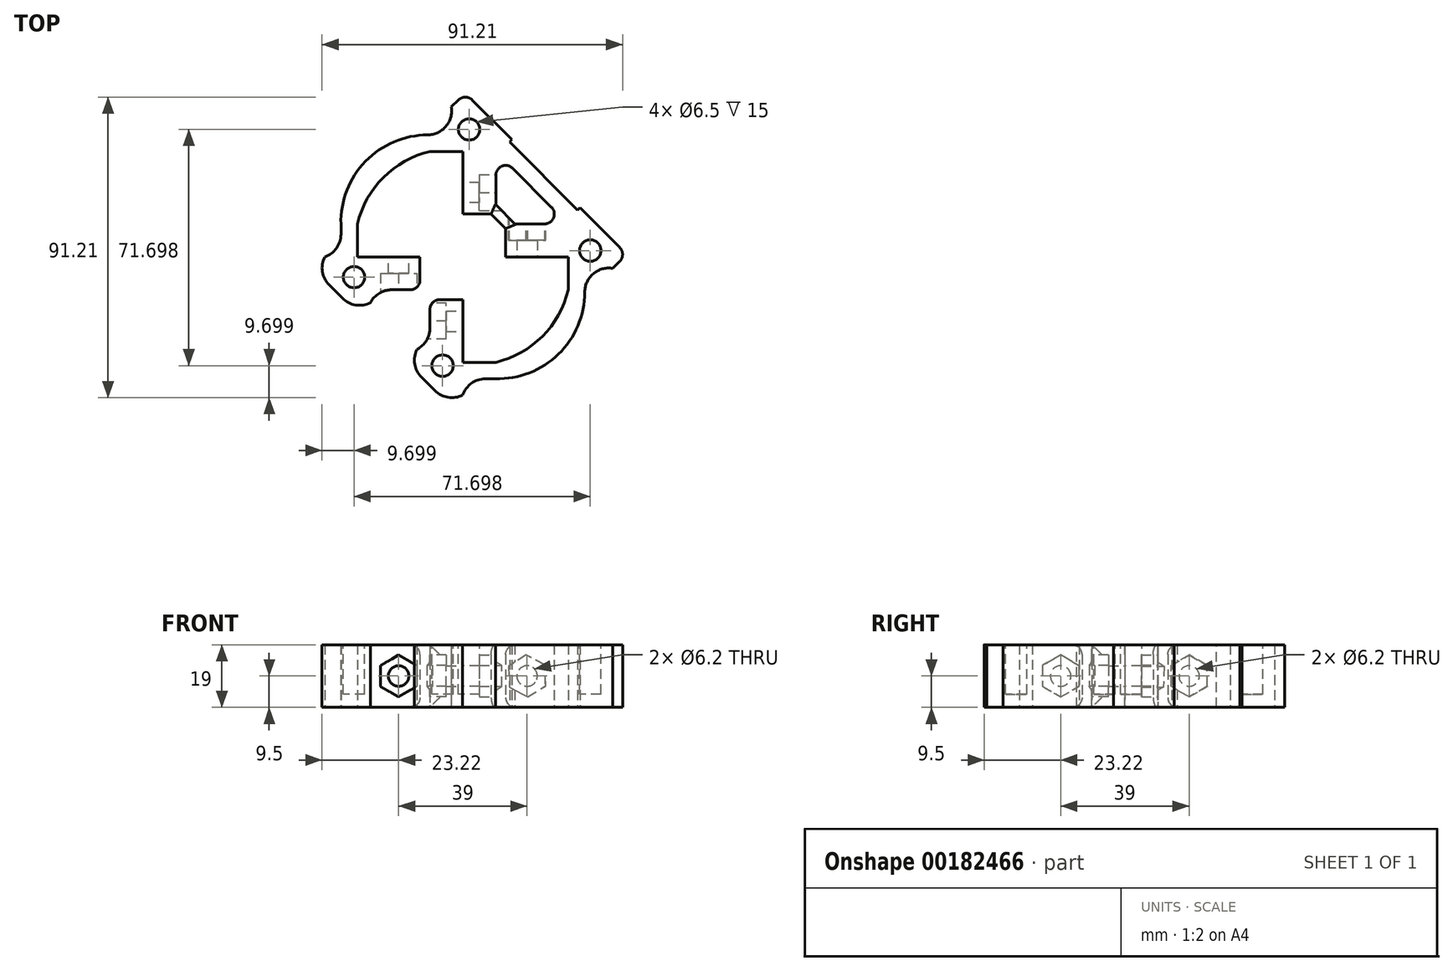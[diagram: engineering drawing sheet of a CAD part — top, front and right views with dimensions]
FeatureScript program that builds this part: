
annotation { "Feature Type Name" : "Feature", "Feature Type Description" : "" }
export const myFeature = defineFeature(function(context is Context, id is Id, definition is map)
    precondition{}
    {
        {
            var Q0;
            Q0=qCreatedBy(makeId("Top.planeOp"),FACE);
            var sketch = newSketch(context, id + "F0", { "sketchPlane" : qUnion([Q0])});
            skLineSegment(sketch, "E0.bottom", {"start": v(13, 13) * mm, "end": v(-13, 13) * mm, "construction": true});
            skLineSegment(sketch, "E0.top", {"start": v(13, -13) * mm, "end": v(-13, -13) * mm, "construction": true});
            skLineSegment(sketch, "E0.left", {"start": v(13, 13) * mm, "end": v(13, -13) * mm, "construction": true});
            skLineSegment(sketch, "E0.right", {"start": v(-13, 13) * mm, "end": v(-13, -13) * mm, "construction": true});
            skPoint(sketch, "E0.middle", {"position": v(0, 0) * mm});
            skLineSegment(sketch, "E1.bottom", {"start": v(13, 0) * mm, "end": v(32, 0) * mm});
            skLineSegment(sketch, "E1.top", {"start": v(13, 10) * mm, "end": v(32, 10) * mm});
            skLineSegment(sketch, "E1.left", {"start": v(13, 0) * mm, "end": v(13, 10) * mm});
            skLineSegment(sketch, "E1.right", {"start": v(32, 0) * mm, "end": v(32, 10) * mm});
            skLineSegment(sketch, "E2.bottom", {"start": v(0, 13) * mm, "end": v(10, 13) * mm});
            skLineSegment(sketch, "E2.top", {"start": v(0, 32) * mm, "end": v(10, 32) * mm});
            skLineSegment(sketch, "E2.left", {"start": v(0, 13) * mm, "end": v(0, 32) * mm});
            skLineSegment(sketch, "E2.right", {"start": v(10, 13) * mm, "end": v(10, 32) * mm});
            skLineSegment(sketch, "E3.bottom", {"start": v(0, -13) * mm, "end": v(-10, -13) * mm});
            skLineSegment(sketch, "E3.top", {"start": v(0, -32) * mm, "end": v(-10, -32) * mm});
            skLineSegment(sketch, "E3.left", {"start": v(0, -13) * mm, "end": v(0, -32) * mm});
            skLineSegment(sketch, "E3.right", {"start": v(-10, -13) * mm, "end": v(-10, -32) * mm});
            skLineSegment(sketch, "E4.bottom", {"start": v(-13, 0) * mm, "end": v(-32, 0) * mm});
            skLineSegment(sketch, "E4.top", {"start": v(-13, -10) * mm, "end": v(-32, -10) * mm});
            skLineSegment(sketch, "E4.left", {"start": v(-13, 0) * mm, "end": v(-13, -10) * mm});
            skLineSegment(sketch, "E4.right", {"start": v(-32, 0) * mm, "end": v(-32, -10) * mm});
            skLineSegment(sketch, "E5", {"start": v(32, 0) * mm, "end": v(32, -10) * mm});
            skLineSegment(sketch, "E6", {"start": v(0, -32) * mm, "end": v(10, -32) * mm});
            skLineSegment(sketch, "E7", {"start": v(-32, 0) * mm, "end": v(-32, 10) * mm});
            skLineSegment(sketch, "E8", {"start": v(0, 32) * mm, "end": v(-10, 32) * mm});
            skArc(sketch, "E9", {"start": v(10, -32) * mm, "mid": v(25.74, -25.74) * mm, "end": v(32, -10) * mm, "construction": true});
            skArc(sketch, "E10", {"start": v(-10, 32) * mm, "mid": v(-25.74, 25.74) * mm, "end": v(-32, 10) * mm, "construction": true});
            skCircle(sketch, "E11", {"center": v(0, 0) * mm, "radius": 15 * mm, "construction": true});
            skLineSegment(sketch, "E12", {"start": v(10, 32) * mm, "end": v(32, 10) * mm});
            skLineSegment(sketch, "E13", {"start": v(-32, -10) * mm, "end": v(-10, -32) * mm});
            skLineSegment(sketch, "E14.0", {"start": v(-37, 0) * mm, "end": v(-37, -12.07) * mm});
            skLineSegment(sketch, "E14.1", {"start": v(37, 0) * mm, "end": v(37, -9.93) * mm});
            skArc(sketch, "E14.2", {"start": v(9.93, -37) * mm, "mid": v(29.28, -29.28) * mm, "end": v(37, -9.93) * mm});
            skLineSegment(sketch, "E14.3", {"start": v(0, -37) * mm, "end": v(9.93, -37) * mm});
            skLineSegment(sketch, "E14.4", {"start": v(0, -37) * mm, "end": v(-12.07, -37) * mm});
            skLineSegment(sketch, "E14.5", {"start": v(37, 0) * mm, "end": v(37, 12.07) * mm});
            skLineSegment(sketch, "E14.6", {"start": v(-37, -12.07) * mm, "end": v(-12.07, -37) * mm});
            skLineSegment(sketch, "E14.7", {"start": v(12.07, 37) * mm, "end": v(37, 12.07) * mm});
            skLineSegment(sketch, "E14.8", {"start": v(0, 37) * mm, "end": v(12.07, 37) * mm});
            skLineSegment(sketch, "E14.9", {"start": v(0, 37) * mm, "end": v(-9.93, 37) * mm});
            skArc(sketch, "E14.10", {"start": v(-9.93, 37) * mm, "mid": v(-29.28, 29.28) * mm, "end": v(-37, 9.93) * mm});
            skLineSegment(sketch, "E14.11", {"start": v(-37, 0) * mm, "end": v(-37, 9.93) * mm});
            skCircle(sketch, "E15", {"center": v(0, 0) * mm, "radius": 4.5 * mm, "construction": true});
            skArc(sketch, "E16", {"start": v(-10, 32) * mm, "mid": v(-24.12, 24.12) * mm, "end": v(-32, 10) * mm});
            skArc(sketch, "E17", {"start": v(10, -32) * mm, "mid": v(24.12, -24.12) * mm, "end": v(32, -10) * mm});
            skLineSegment(sketch, "E18", {"start": v(10, 13) * mm, "end": v(13, 10) * mm, "construction": true});
            skLineSegment(sketch, "E19", {"start": v(10, 15.83) * mm, "end": v(15.83, 10) * mm});
            skLineSegment(sketch, "E20", {"start": v(8.59, 13) * mm, "end": v(13, 8.59) * mm});
            skLineSegment(sketch, "E21", {"start": v(-21, -21) * mm, "end": v(-24.54, -24.54) * mm, "construction": true});
            skLineSegment(sketch, "E22.0", {"start": v(-28.07, -13.93) * mm, "end": v(-31.6, -17.46) * mm});
            skLineSegment(sketch, "E23.0", {"start": v(-13.93, -28.07) * mm, "end": v(-17.46, -31.6) * mm});
            skLineSegment(sketch, "E24", {"start": v(37, 12.07) * mm, "end": v(49.02, 0.05) * mm});
            skLineSegment(sketch, "E25", {"start": v(49.02, 0.05) * mm, "end": v(45.49, -3.49) * mm});
            skLineSegment(sketch, "E26", {"start": v(45.49, -3.49) * mm, "end": v(32, 10) * mm});
            skLineSegment(sketch, "E27", {"start": v(12.07, 37) * mm, "end": v(0.05, 49.02) * mm});
            skLineSegment(sketch, "E28", {"start": v(0.05, 49.02) * mm, "end": v(-3.49, 45.49) * mm});
            skLineSegment(sketch, "E29", {"start": v(-3.49, 45.49) * mm, "end": v(10, 32) * mm});
            skLineSegment(sketch, "E30", {"start": v(-12.07, -37) * mm, "end": v(-3.59, -45.49) * mm});
            skLineSegment(sketch, "E31", {"start": v(-3.59, -45.49) * mm, "end": v(-0.05, -41.95) * mm});
            skLineSegment(sketch, "E32", {"start": v(-0.05, -41.95) * mm, "end": v(-10, -32) * mm});
            skLineSegment(sketch, "E33", {"start": v(-37, -12.07) * mm, "end": v(-45.49, -3.59) * mm});
            skLineSegment(sketch, "E34", {"start": v(-45.49, -3.59) * mm, "end": v(-41.95, -0.05) * mm});
            skLineSegment(sketch, "E35", {"start": v(-41.95, -0.05) * mm, "end": v(-32, -10) * mm});
            skSolve(sketch);
        }
        {
            var Q0;
            Q0=makeQuery(id+"F0.imprint","IMPRINT",FACE,{"disambiguationData":[TD([[makeQuery(id+"F0.imprint","IMPRINT",EDGE,{"derivedFrom":sQuery(id+"F0.wireOp",EDGE,"E1.right")}),-1.0]])]});
            var Q1;
            Q1=makeQuery(id+"F0.imprint","IMPRINT",FACE,{"disambiguationData":[TD([[makeQuery(id+"F0.imprint","IMPRINT",EDGE,{"derivedFrom":sQuery(id+"F0.wireOp",EDGE,"E3.bottom")}),1.0]])]});
            var Q2;
            Q2=makeQuery(id+"F0.imprint","IMPRINT",FACE,{"disambiguationData":[TD([[makeQuery(id+"F0.imprint","IMPRINT",EDGE,{"derivedFrom":sQuery(id+"F0.wireOp",EDGE,"E1.bottom")}),1.0]])]});
            var Q3;
            Q3=makeQuery(id+"F0.imprint","IMPRINT",FACE,{"disambiguationData":[TD([[makeQuery(id+"F0.imprint","IMPRINT",EDGE,{"derivedFrom":sQuery(id+"F0.wireOp",EDGE,"E2.bottom")}),1.0]])]});
            var Q4;
            Q4=makeQuery(id+"F0.imprint","IMPRINT",FACE,{"disambiguationData":[TD([[makeQuery(id+"F0.imprint","IMPRINT",EDGE,{"derivedFrom":sQuery(id+"F0.wireOp",EDGE,"E4.bottom")}),1.0]])]});
            var Q5;
            {var subQ4=sQuery(id+"F0.wireOp",EDGE,"7QYkWqvo-aJCI-HwU7-Pkr0-dl33K8GSCUU7");Q5=makeQuery(id+"F0.imprint","IMPRINT",FACE,{"disambiguationData":[TD([[makeQuery(id+"F0.imprint","IMPRINT",EDGE,{"derivedFrom":subQ4}),-1.0]])]});}
            var Q6;
            {var subQ4=sQuery(id+"F0.wireOp",EDGE,"jUQw4thv-zTIx-3EJl-gbHM-SSJWuM9t6vhC");Q6=makeQuery(id+"F0.imprint","IMPRINT",FACE,{"disambiguationData":[TD([[makeQuery(id+"F0.imprint","IMPRINT",EDGE,{"derivedFrom":subQ4}),1.0]])]});}
            var Q7;
            {var subQ3=sQuery(id+"F0.wireOp",EDGE,"E19");Q7=makeQuery(id+"F0.imprint","IMPRINT",FACE,{"disambiguationData":[TD([[makeQuery(id+"F0.imprint","IMPRINT",EDGE,{"derivedFrom":subQ3}),-1.0]])]});}
            var Q8;
            {var subQ4=sQuery(id+"F0.wireOp",EDGE,"E12");Q8=makeQuery(id+"F0.imprint","IMPRINT",FACE,{"disambiguationData":[TD([[makeQuery(id+"F0.imprint","IMPRINT",EDGE,{"derivedFrom":subQ4}),1.0]])]});}
            var Q9;
            {var subQ0=sQuery(id+"F0.wireOp",EDGE,"E27");Q9=makeQuery(id+"F0.imprint","IMPRINT",FACE,{"disambiguationData":[TD([[makeQuery(id+"F0.imprint","IMPRINT",EDGE,{"derivedFrom":subQ0}),1.0]])]});}
            var Q10;
            {var subQ7=sQuery(id+"F0.wireOp",EDGE,"E2.top");Q10=makeQuery(id+"F0.imprint","IMPRINT",FACE,{"disambiguationData":[TD([[makeQuery(id+"F0.imprint","IMPRINT",EDGE,{"derivedFrom":subQ7}),1.0]])]});}
            var Q11;
            {var subQ0=sQuery(id+"F0.wireOp",EDGE,"E24");Q11=makeQuery(id+"F0.imprint","IMPRINT",FACE,{"disambiguationData":[TD([[makeQuery(id+"F0.imprint","IMPRINT",EDGE,{"derivedFrom":subQ0}),-1.0]])]});}
            var Q12;
            {var subQ0=sQuery(id+"F0.wireOp",EDGE,"E30");Q12=makeQuery(id+"F0.imprint","IMPRINT",FACE,{"disambiguationData":[TD([[makeQuery(id+"F0.imprint","IMPRINT",EDGE,{"derivedFrom":subQ0}),1.0]])]});}
            var Q13;
            {var subQ0=sQuery(id+"F0.wireOp",EDGE,"E33");Q13=makeQuery(id+"F0.imprint","IMPRINT",FACE,{"disambiguationData":[TD([[makeQuery(id+"F0.imprint","IMPRINT",EDGE,{"derivedFrom":subQ0}),-1.0]])]});}
            var Q14;
            {var subQ3=sQuery(id+"F0.wireOp",EDGE,"E23.0");Q14=makeQuery(id+"F0.imprint","IMPRINT",FACE,{"disambiguationData":[TD([[makeQuery(id+"F0.imprint","IMPRINT",EDGE,{"derivedFrom":subQ3}),1.0]])]});}
            var Q15;
            {var subQ0=sQuery(id+"F0.wireOp",EDGE,"E22.0");Q15=makeQuery(id+"F0.imprint","IMPRINT",FACE,{"disambiguationData":[TD([[makeQuery(id+"F0.imprint","IMPRINT",EDGE,{"derivedFrom":subQ0}),-1.0]])]});}
            extrude(context, id + "F1", {"entities" : qUnion([Q0, Q1, Q2, Q3, Q4, Q5, Q6, Q7, Q8, Q9, Q10, Q11, Q12, Q13, Q14, Q15]), "depth" : 19 * mm});
        }
        {
            var Q0;
            Q0=makeQuery(id+"F1.opExtrude","SWEPT_FACE",FACE,{"disambiguationData":[OSD([sQuery(id+"F0.wireOp",EDGE,"E3.right")])]});
            var sketch = newSketch(context, id + "F2", { "sketchPlane" : qUnion([Q0])});
            skLineSegment(sketch, "E36", {"start": v(19.5, 9.5) * mm, "end": v(32, 9.5) * mm, "construction": true});
            skCircle(sketch, "E37.cCircle", {"center": v(19.5, 9.5) * mm, "radius": 5.5 * mm, "construction": true});
            skLineSegment(sketch, "E37.0", {"start": v(14, 6.32) * mm, "end": v(14, 12.68) * mm});
            skLineSegment(sketch, "E37.1", {"start": v(14, 12.68) * mm, "end": v(19.5, 15.85) * mm});
            skLineSegment(sketch, "E37.2", {"start": v(19.5, 15.85) * mm, "end": v(25, 12.68) * mm});
            skLineSegment(sketch, "E37.3", {"start": v(25, 12.68) * mm, "end": v(25, 6.32) * mm});
            skLineSegment(sketch, "E37.4", {"start": v(25, 6.32) * mm, "end": v(19.5, 3.15) * mm});
            skLineSegment(sketch, "E37.5", {"start": v(19.5, 3.15) * mm, "end": v(14, 6.32) * mm});
            skPoint(sketch, "E37.0.midPoint", {"position": v(14, 9.5) * mm});
            skSolve(sketch);
        }
        {
            var Q0;
            Q0=makeQuery(id+"F2.imprint","IMPRINT",FACE,{"disambiguationData":[TD([[makeQuery(id+"F2.imprint","IMPRINT",EDGE,{"derivedFrom":sQuery(id+"F2.wireOp",EDGE,"E37.0")}),-1.0]])]});
            extrude(context, id + "F3", {"entities" : qUnion([Q0]), "operationType" : NewBodyOperationType.REMOVE, "oppositeDirection" : true, "depth" : 5 * mm});
        }
        {
            var Q0;
            Q0=makeQuery(id+"F1.opExtrude","SWEPT_FACE",FACE,{"disambiguationData":[OSD([sQuery(id+"F0.wireOp",EDGE,"E4.top")])]});
            var sketch = newSketch(context, id + "F4", { "sketchPlane" : qUnion([Q0])});
            skLineSegment(sketch, "E38", {"start": v(-32, 9.5) * mm, "end": v(-19.5, 9.5) * mm, "construction": true});
            skPoint(sketch, "E38.endSnap0", {"position": v(-32, 9.5) * mm});
            skCircle(sketch, "E39.cCircle", {"center": v(-19.5, 9.5) * mm, "radius": 5.5 * mm, "construction": true});
            skLineSegment(sketch, "E39.0", {"start": v(-14, 12.68) * mm, "end": v(-14, 6.32) * mm});
            skLineSegment(sketch, "E39.1", {"start": v(-14, 6.32) * mm, "end": v(-19.5, 3.15) * mm});
            skLineSegment(sketch, "E39.2", {"start": v(-19.5, 3.15) * mm, "end": v(-25, 6.32) * mm});
            skLineSegment(sketch, "E39.3", {"start": v(-25, 6.32) * mm, "end": v(-25, 12.68) * mm});
            skLineSegment(sketch, "E39.4", {"start": v(-25, 12.68) * mm, "end": v(-19.5, 15.85) * mm});
            skLineSegment(sketch, "E39.5", {"start": v(-19.5, 15.85) * mm, "end": v(-14, 12.68) * mm});
            skPoint(sketch, "E39.0.midPoint", {"position": v(-14, 9.5) * mm});
            skSolve(sketch);
        }
        {
            var Q0;
            Q0=makeQuery(id+"F4.imprint","IMPRINT",FACE,{"disambiguationData":[TD([[makeQuery(id+"F4.imprint","IMPRINT",EDGE,{"derivedFrom":sQuery(id+"F4.wireOp",EDGE,"E39.0")}),-1.0]])]});
            extrude(context, id + "F5", {"entities" : qUnion([Q0]), "operationType" : NewBodyOperationType.REMOVE, "oppositeDirection" : true, "depth" : 5 * mm});
        }
        {
            var Q0;
            Q0=makeQuery(id+"F1.opExtrude","SWEPT_FACE",FACE,{"disambiguationData":[OSD([sQuery(id+"F0.wireOp",EDGE,"E2.right")])]});
            var sketch = newSketch(context, id + "F6", { "sketchPlane" : qUnion([Q0])});
            skCircle(sketch, "E40.cCircle", {"center": v(19.5, 9.5) * mm, "radius": 5.5 * mm, "construction": true});
            skLineSegment(sketch, "E40.0", {"start": v(14, 6.32) * mm, "end": v(14, 12.68) * mm});
            skLineSegment(sketch, "E40.1", {"start": v(14, 12.68) * mm, "end": v(19.5, 15.85) * mm});
            skLineSegment(sketch, "E40.2", {"start": v(19.5, 15.85) * mm, "end": v(25, 12.68) * mm});
            skLineSegment(sketch, "E40.3", {"start": v(25, 12.68) * mm, "end": v(25, 6.32) * mm});
            skLineSegment(sketch, "E40.4", {"start": v(25, 6.32) * mm, "end": v(19.5, 3.15) * mm});
            skLineSegment(sketch, "E40.5", {"start": v(19.5, 3.15) * mm, "end": v(14, 6.32) * mm});
            skPoint(sketch, "E40.0.midPoint", {"position": v(14, 9.5) * mm});
            skSolve(sketch);
        }
        {
            var Q0;
            Q0=makeQuery(id+"F6.imprint","IMPRINT",FACE,{"disambiguationData":[TD([[makeQuery(id+"F6.imprint","IMPRINT",EDGE,{"derivedFrom":sQuery(id+"F6.wireOp",EDGE,"E40.0")}),-1.0]])]});
            var Q1;
            {var subQ1=sQuery(id+"F6.wireOp",EDGE,"E40.2");Q1=makeQuery(id+"F6.imprint","IMPRINT",FACE,{"disambiguationData":[TD([[makeQuery(id+"F6.imprint","IMPRINT",EDGE,{"derivedFrom":subQ1}),-1.0]])]});}
            extrude(context, id + "F7", {"entities" : qUnion([Q0, Q1]), "operationType" : NewBodyOperationType.REMOVE, "oppositeDirection" : true, "depth" : 10 * mm, "symmetric" : true});
        }
        {
            var Q0;
            Q0=makeQuery(id+"F1.opExtrude","SWEPT_FACE",FACE,{"disambiguationData":[OSD([sQuery(id+"F0.wireOp",EDGE,"E1.top")])]});
            var sketch = newSketch(context, id + "F8", { "sketchPlane" : qUnion([Q0])});
            skLineSegment(sketch, "E41", {"start": v(-32, 9.5) * mm, "end": v(-19.5, 9.5) * mm, "construction": true});
            skCircle(sketch, "E42.cCircle", {"center": v(-19.5, 9.5) * mm, "radius": 5.5 * mm, "construction": true});
            skLineSegment(sketch, "E42.0", {"start": v(-13.87, 12.45) * mm, "end": v(-14.13, 6.1) * mm});
            skLineSegment(sketch, "E42.1", {"start": v(-14.13, 6.1) * mm, "end": v(-19.76, 3.15) * mm});
            skLineSegment(sketch, "E42.2", {"start": v(-19.76, 3.15) * mm, "end": v(-25.13, 6.55) * mm});
            skLineSegment(sketch, "E42.3", {"start": v(-25.13, 6.55) * mm, "end": v(-24.87, 12.9) * mm});
            skLineSegment(sketch, "E42.4", {"start": v(-24.87, 12.9) * mm, "end": v(-19.24, 15.85) * mm});
            skLineSegment(sketch, "E42.5", {"start": v(-19.24, 15.85) * mm, "end": v(-13.87, 12.45) * mm});
            skPoint(sketch, "E42.0.midPoint", {"position": v(-14, 9.27) * mm});
            skSolve(sketch);
        }
        {
            var Q0;
            Q0=makeQuery(id+"F8.imprint","IMPRINT",FACE,{"disambiguationData":[TD([[makeQuery(id+"F8.imprint","IMPRINT",EDGE,{"derivedFrom":sQuery(id+"F8.wireOp",EDGE,"E42.0")}),-1.0]])]});
            var Q1;
            {var subQ6=sQuery(id+"F8.wireOp",EDGE,"E42.2");Q1=makeQuery(id+"F8.imprint","IMPRINT",FACE,{"disambiguationData":[TD([[makeQuery(id+"F8.imprint","IMPRINT",EDGE,{"derivedFrom":subQ6}),-1.0]])]});}
            extrude(context, id + "F9", {"entities" : qUnion([Q0, Q1]), "operationType" : NewBodyOperationType.REMOVE, "oppositeDirection" : true, "depth" : 10 * mm, "symmetric" : true});
        }
        {
            var Q0;
            Q0=sQuery(id+"F6.wireOp",VERTEX,"E40.cCircle.center");
            var Q1;
            Q1=sQuery(id+"F8.wireOp",VERTEX,"E41.end");
            var Q2;
            Q2=sQuery(id+"F2.wireOp",VERTEX,"E37.cCircle.center");
            var Q3;
            Q3=sQuery(id+"F4.wireOp",VERTEX,"E38.end");
            var Q4;
            Q4=makeQuery(id+"F1.opExtrude","SWEPT_BODY",BODY,{"disambiguationData":[OSD([sQuery(id+"F0.wireOp",EDGE,"E1.bottom"),sQuery(id+"F0.wireOp",EDGE,"E1.top"),sQuery(id+"F0.wireOp",EDGE,"E1.left"),sQuery(id+"F0.wireOp",EDGE,"E2.bottom"),sQuery(id+"F0.wireOp",EDGE,"E2.left"),sQuery(id+"F0.wireOp",EDGE,"E2.right"),sQuery(id+"F0.wireOp",EDGE,"E3.bottom"),sQuery(id+"F0.wireOp",EDGE,"E3.left"),sQuery(id+"F0.wireOp",EDGE,"E3.right"),sQuery(id+"F0.wireOp",EDGE,"E4.bottom"),sQuery(id+"F0.wireOp",EDGE,"E4.top"),sQuery(id+"F0.wireOp",EDGE,"E4.left"),sQuery(id+"F0.wireOp",EDGE,"E5"),sQuery(id+"F0.wireOp",EDGE,"E6"),sQuery(id+"F0.wireOp",EDGE,"E7"),sQuery(id+"F0.wireOp",EDGE,"E8"),sQuery(id+"F0.wireOp",EDGE,"E12"),sQuery(id+"F0.wireOp",EDGE,"E13"),sQuery(id+"F0.wireOp",EDGE,"E14.0"),sQuery(id+"F0.wireOp",EDGE,"E14.1"),sQuery(id+"F0.wireOp",EDGE,"E14.2"),sQuery(id+"F0.wireOp",EDGE,"E14.3"),sQuery(id+"F0.wireOp",EDGE,"E14.4"),sQuery(id+"F0.wireOp",EDGE,"E14.5"),sQuery(id+"F0.wireOp",EDGE,"E14.6"),sQuery(id+"F0.wireOp",EDGE,"E14.7"),sQuery(id+"F0.wireOp",EDGE,"E14.8"),sQuery(id+"F0.wireOp",EDGE,"E14.9"),sQuery(id+"F0.wireOp",EDGE,"E14.10"),sQuery(id+"F0.wireOp",EDGE,"E14.11"),sQuery(id+"F0.wireOp",EDGE,"E16"),sQuery(id+"F0.wireOp",EDGE,"E17"),sQuery(id+"F0.wireOp",EDGE,"E19"),sQuery(id+"F0.wireOp",EDGE,"E20"),sQuery(id+"F0.wireOp",EDGE,"E22.0"),sQuery(id+"F0.wireOp",EDGE,"E23.0"),sQuery(id+"F0.wireOp",EDGE,"7QYkWqvo-aJCI-HwU7-Pkr0-dl33K8GSCUU7"),sQuery(id+"F0.wireOp",EDGE,"UtTPwMuY-yqNM-BxKw-NphB-S71OTgtlkQoO"),sQuery(id+"F0.wireOp",EDGE,"jUQw4thv-zTIx-3EJl-gbHM-SSJWuM9t6vhC"),sQuery(id+"F0.wireOp",EDGE,"jgdTeO3I-7sCt-ISHI-VTCF-wijFFm9s4p1R"),sQuery(id+"F0.wireOp",EDGE,"E24"),sQuery(id+"F0.wireOp",EDGE,"E25"),sQuery(id+"F0.wireOp",EDGE,"E26"),sQuery(id+"F0.wireOp",EDGE,"E27"),sQuery(id+"F0.wireOp",EDGE,"E28"),sQuery(id+"F0.wireOp",EDGE,"E29")])]});
            hole(context, id + "F10", {"style" : HoleStyle.SIMPLE, "endStyle" : HoleEndStyle.BLIND, "holeDiameter" : 6.2 * mm, "holeDepth" : 10 * mm, "locations" : qUnion([Q0, Q1, Q2, Q3]), "scope" : qUnion([Q4])});
        }
        {
            var Q0;
            Q0=makeQuery(id+"F1.opExtrude","SWEPT_FACE",FACE,{"disambiguationData":[OSD([sQuery(id+"F0.wireOp",EDGE,"E14.7"),sQuery(id+"F0.wireOp",EDGE,"E24"),sQuery(id+"F0.wireOp",EDGE,"E27")])]});
            var sketch = newSketch(context, id + "F11", { "sketchPlane" : qUnion([Q0])});
            skLineSegment(sketch, "E43", {"start": v(-34.63, 19) * mm, "end": v(-34.63, 0) * mm});
            skLineSegment(sketch, "E44", {"start": v(34.63, 0) * mm, "end": v(34.63, 19) * mm});
            skLineSegment(sketch, "E45", {"start": v(-14.63, 19) * mm, "end": v(-14.63, 0) * mm});
            skLineSegment(sketch, "E46", {"start": v(14.63, 19) * mm, "end": v(14.63, 0) * mm});
            skSolve(sketch);
        }
        {
            var Q0;
            {var subQ0=sQuery(id+"F11.wireOp",EDGE,"E44");Q0=makeQuery(id+"F11.imprint","IMPRINT",FACE,{"disambiguationData":[TD([[makeQuery(id+"F11.imprint","IMPRINT",EDGE,{"derivedFrom":subQ0}),-1.0]])]});}
            var Q1;
            {var subQ0=sQuery(id+"F11.wireOp",EDGE,"E43");Q1=makeQuery(id+"F11.imprint","IMPRINT",FACE,{"disambiguationData":[TD([[makeQuery(id+"F11.imprint","IMPRINT",EDGE,{"derivedFrom":subQ0}),1.0]])]});}
            extrude(context, id + "F12", {"entities" : qUnion([Q0, Q1]), "operationType" : NewBodyOperationType.ADD, "depth" : 1 * mm});
        }
        {
            var Q0;
            Q0=makeQuery(id+"F1.opExtrude","SWEPT_EDGE",EDGE,{"disambiguationData":[OSD([sQuery(id+"F0.wireOp",EDGE,"E14.8"),sQuery(id+"F0.wireOp",EDGE,"E29")])]});
            var Q1;
            Q1=makeQuery(id+"F1.opExtrude","SWEPT_EDGE",EDGE,{"disambiguationData":[OSD([sQuery(id+"F0.wireOp",EDGE,"E14.5"),sQuery(id+"F0.wireOp",EDGE,"E26")])]});
            var Q2;
            Q2=makeQuery(id+"F12.opExtrude","CAP_EDGE",EDGE,{"disambiguationData":[OSD([sQuery(id+"F11.wireOp",EDGE,"E46")])],"isStart":true});
            var Q3;
            Q3=makeQuery(id+"F12.opExtrude","CAP_EDGE",EDGE,{"disambiguationData":[OSD([sQuery(id+"F11.wireOp",EDGE,"E45")])],"isStart":true});
            var Q4;
            Q4=makeQuery(id+"F1.opExtrude","SWEPT_EDGE",EDGE,{"disambiguationData":[OSD([sQuery(id+"F0.wireOp",EDGE,"E14.4"),sQuery(id+"F0.wireOp",EDGE,"E32")])]});
            var Q5;
            Q5=makeQuery(id+"F1.opExtrude","SWEPT_EDGE",EDGE,{"disambiguationData":[OSD([sQuery(id+"F0.wireOp",EDGE,"E14.0"),sQuery(id+"F0.wireOp",EDGE,"E35")])]});
            var Q6;
            Q6=makeQuery(id+"F1.opExtrude","SWEPT_EDGE",EDGE,{"disambiguationData":[OSD([sQuery(id+"F0.wireOp",EDGE,"E33"),sQuery(id+"F0.wireOp",EDGE,"E34")])]});
            var Q7;
            Q7=makeQuery(id+"F1.opExtrude","SWEPT_EDGE",EDGE,{"disambiguationData":[OSD([sQuery(id+"F0.wireOp",EDGE,"E14.6"),sQuery(id+"F0.wireOp",EDGE,"E22.0")])]});
            var Q8;
            Q8=makeQuery(id+"F1.opExtrude","SWEPT_EDGE",EDGE,{"disambiguationData":[OSD([sQuery(id+"F0.wireOp",EDGE,"E4.top"),sQuery(id+"F0.wireOp",EDGE,"E4.right"),sQuery(id+"F0.wireOp",EDGE,"E13"),sQuery(id+"F0.wireOp",EDGE,"E35")])]});
            var Q9;
            Q9=makeQuery(id+"F1.opExtrude","SWEPT_EDGE",EDGE,{"disambiguationData":[OSD([sQuery(id+"F0.wireOp",EDGE,"E3.top"),sQuery(id+"F0.wireOp",EDGE,"E3.right"),sQuery(id+"F0.wireOp",EDGE,"E13"),sQuery(id+"F0.wireOp",EDGE,"E32")])]});
            var Q10;
            Q10=makeQuery(id+"F1.opExtrude","SWEPT_EDGE",EDGE,{"disambiguationData":[OSD([sQuery(id+"F0.wireOp",EDGE,"E14.6"),sQuery(id+"F0.wireOp",EDGE,"E23.0")])]});
            var Q11;
            Q11=makeQuery(id+"F1.opExtrude","SWEPT_EDGE",EDGE,{"disambiguationData":[OSD([sQuery(id+"F0.wireOp",EDGE,"E30"),sQuery(id+"F0.wireOp",EDGE,"E31")])]});
            fillet(context, id + "F13", {"entities" : qUnion([Q0, Q1, Q2, Q3, Q4, Q5, Q6, Q7, Q8, Q9, Q10, Q11]), "radius" : 7.3 * mm, "tangentPropagation" : true, "allowEdgeOverflow" : false});
        }
        {
            var Q0;
            Q0=makeQuery(id+"F1.opExtrude","CAP_EDGE",EDGE,{"disambiguationData":[OSD([sQuery(id+"F0.wireOp",EDGE,"E4.left")])],"isStart":true});
            var Q1;
            Q1=makeQuery(id+"F1.opExtrude","CAP_EDGE",EDGE,{"disambiguationData":[OSD([sQuery(id+"F0.wireOp",EDGE,"E3.bottom")])],"isStart":false});
            var Q2;
            Q2=makeQuery(id+"F1.opExtrude","CAP_EDGE",EDGE,{"disambiguationData":[OSD([sQuery(id+"F0.wireOp",EDGE,"E4.left")])],"isStart":false});
            var Q3;
            Q3=makeQuery(id+"F1.opExtrude","CAP_EDGE",EDGE,{"disambiguationData":[OSD([sQuery(id+"F0.wireOp",EDGE,"E3.bottom")])],"isStart":true});
            var Q4;
            Q4=makeQuery(id+"F1.opExtrude","CAP_EDGE",EDGE,{"disambiguationData":[OSD([sQuery(id+"F0.wireOp",EDGE,"E2.bottom")])],"isStart":false});
            var Q5;
            Q5=makeQuery(id+"F1.opExtrude","CAP_EDGE",EDGE,{"disambiguationData":[OSD([sQuery(id+"F0.wireOp",EDGE,"E20")])],"isStart":false});
            var Q6;
            Q6=makeQuery(id+"F1.opExtrude","CAP_EDGE",EDGE,{"disambiguationData":[OSD([sQuery(id+"F0.wireOp",EDGE,"E1.left")])],"isStart":false});
            var Q7;
            Q7=makeQuery(id+"F1.opExtrude","CAP_EDGE",EDGE,{"disambiguationData":[OSD([sQuery(id+"F0.wireOp",EDGE,"E1.left")])],"isStart":true});
            var Q8;
            Q8=makeQuery(id+"F1.opExtrude","CAP_EDGE",EDGE,{"disambiguationData":[OSD([sQuery(id+"F0.wireOp",EDGE,"E20")])],"isStart":true});
            var Q9;
            {var subQ0=sQuery(id+"F11.wireOp",EDGE,"E45");Q9=makeQuery(id+"F13.opFillet","BLEND_EDGE",EDGE,{"blendedFrom":[makeQuery(id+"F12.opExtrude","CAP_EDGE",EDGE,{"disambiguationData":[OSD([subQ0])],"isStart":true}),makeQuery(id+"F12.opExtrude","CAP_FACE",FACE,{"disambiguationData":[OSD([sQuery(id+"F0.wireOp",EDGE,"E14.7"),sQuery(id+"F0.wireOp",EDGE,"E24"),sQuery(id+"F0.wireOp",EDGE,"E27"),sQuery(id+"F11.wireOp",EDGE,"E43"),subQ0])],"isStart":false})],"blendedInto":[makeQuery(id+"F12.opExtrude","CAP_FACE",FACE,{"disambiguationData":[OSD([sQuery(id+"F0.wireOp",EDGE,"E14.7"),sQuery(id+"F0.wireOp",EDGE,"E24"),sQuery(id+"F0.wireOp",EDGE,"E27"),sQuery(id+"F11.wireOp",EDGE,"E43"),subQ0])],"isStart":false})]});}
            var Q10;
            {var subQ0=sQuery(id+"F11.wireOp",EDGE,"E46");Q10=makeQuery(id+"F13.opFillet","BLEND_EDGE",EDGE,{"blendedFrom":[makeQuery(id+"F12.opExtrude","CAP_EDGE",EDGE,{"disambiguationData":[OSD([subQ0])],"isStart":true}),makeQuery(id+"F12.opExtrude","CAP_FACE",FACE,{"disambiguationData":[OSD([sQuery(id+"F0.wireOp",EDGE,"E14.7"),sQuery(id+"F0.wireOp",EDGE,"E24"),sQuery(id+"F0.wireOp",EDGE,"E27"),sQuery(id+"F11.wireOp",EDGE,"E44"),subQ0])],"isStart":false})],"blendedInto":[makeQuery(id+"F12.opExtrude","CAP_FACE",FACE,{"disambiguationData":[OSD([sQuery(id+"F0.wireOp",EDGE,"E14.7"),sQuery(id+"F0.wireOp",EDGE,"E24"),sQuery(id+"F0.wireOp",EDGE,"E27"),sQuery(id+"F11.wireOp",EDGE,"E44"),subQ0])],"isStart":false})]});}
            var Q11;
            Q11=makeQuery(id+"F1.opExtrude","SWEPT_EDGE",EDGE,{"disambiguationData":[OSD([sQuery(id+"F0.wireOp",EDGE,"7QYkWqvo-aJCI-HwU7-Pkr0-dl33K8GSCUU7"),sQuery(id+"F0.wireOp",EDGE,"UtTPwMuY-yqNM-BxKw-NphB-S71OTgtlkQoO")])]});
            var Q12;
            Q12=makeQuery(id+"F1.opExtrude","SWEPT_EDGE",EDGE,{"disambiguationData":[OSD([sQuery(id+"F0.wireOp",EDGE,"jUQw4thv-zTIx-3EJl-gbHM-SSJWuM9t6vhC"),sQuery(id+"F0.wireOp",EDGE,"jgdTeO3I-7sCt-ISHI-VTCF-wijFFm9s4p1R")])]});
            var Q13;
            Q13=makeQuery(id+"F1.opExtrude","SWEPT_EDGE",EDGE,{"disambiguationData":[OSD([sQuery(id+"F0.wireOp",EDGE,"E4.top"),sQuery(id+"F0.wireOp",EDGE,"E4.left")])]});
            var Q14;
            Q14=makeQuery(id+"F1.opExtrude","SWEPT_EDGE",EDGE,{"disambiguationData":[OSD([sQuery(id+"F0.wireOp",EDGE,"E3.bottom"),sQuery(id+"F0.wireOp",EDGE,"E3.right")])]});
            var Q15;
            Q15=makeQuery(id+"F1.opExtrude","SWEPT_EDGE",EDGE,{"disambiguationData":[OSD([sQuery(id+"F0.wireOp",EDGE,"E13"),sQuery(id+"F0.wireOp",EDGE,"E22.0")])]});
            var Q16;
            Q16=makeQuery(id+"F1.opExtrude","SWEPT_EDGE",EDGE,{"disambiguationData":[OSD([sQuery(id+"F0.wireOp",EDGE,"E13"),sQuery(id+"F0.wireOp",EDGE,"E23.0")])]});
            var Q17;
            Q17=makeQuery(id+"F12.opExtrude","CAP_EDGE",EDGE,{"disambiguationData":[OSD([sQuery(id+"F11.wireOp",EDGE,"E44")])],"isStart":false});
            var Q18;
            Q18=makeQuery(id+"F12.opExtrude","CAP_EDGE",EDGE,{"disambiguationData":[OSD([sQuery(id+"F11.wireOp",EDGE,"E43")])],"isStart":false});
            var Q19;
            Q19=makeQuery(id+"F1.opExtrude","SWEPT_EDGE",EDGE,{"disambiguationData":[OSD([sQuery(id+"F0.wireOp",EDGE,"E30"),sQuery(id+"F0.wireOp",EDGE,"E31")])]});
            var Q20;
            Q20=makeQuery(id+"F1.opExtrude","SWEPT_EDGE",EDGE,{"disambiguationData":[OSD([sQuery(id+"F0.wireOp",EDGE,"E33"),sQuery(id+"F0.wireOp",EDGE,"E34")])]});
            var Q21;
            Q21=makeQuery(id+"F1.opExtrude","SWEPT_EDGE",EDGE,{"disambiguationData":[OSD([sQuery(id+"F0.wireOp",EDGE,"E2.top"),sQuery(id+"F0.wireOp",EDGE,"E2.right"),sQuery(id+"F0.wireOp",EDGE,"E12"),sQuery(id+"F0.wireOp",EDGE,"E29")])]});
            var Q22;
            Q22=makeQuery(id+"F1.opExtrude","SWEPT_EDGE",EDGE,{"disambiguationData":[OSD([sQuery(id+"F0.wireOp",EDGE,"E1.top"),sQuery(id+"F0.wireOp",EDGE,"E1.right"),sQuery(id+"F0.wireOp",EDGE,"E12"),sQuery(id+"F0.wireOp",EDGE,"E26")])]});
            var Q23;
            Q23=makeQuery(id+"F1.opExtrude","CAP_EDGE",EDGE,{"disambiguationData":[OSD([sQuery(id+"F0.wireOp",EDGE,"E2.bottom")])],"isStart":true});
            fillet(context, id + "F14", {"entities" : qUnion([Q0, Q1, Q2, Q3, Q4, Q5, Q6, Q7, Q8, Q9, Q10, Q11, Q12, Q13, Q14, Q15, Q16, Q17, Q18, Q19, Q20, Q21, Q22, Q23]), "radius" : 3 * mm, "tangentPropagation" : true, "allowEdgeOverflow" : false});
        }
        {
            var Q0;
            {var subQ0=sQuery(id+"F0.wireOp",EDGE,"E27");var subQ1=sQuery(id+"F0.wireOp",EDGE,"E24");var subQ2=sQuery(id+"F0.wireOp",EDGE,"E14.7");var subQ3=makeQuery(id+"F1.opExtrude","CAP_EDGE",EDGE,{"disambiguationData":[OSD([subQ2,subQ1,subQ0])],"isStart":false});Q0=makeQuery(id+"F12.boolean.opBoolean","MERGE",FACE,{"derivedFrom":[makeQuery(id+"F1.opExtrude","CAP_FACE",FACE,{"disambiguationData":[OSD([sQuery(id+"F0.wireOp",EDGE,"E1.bottom"),sQuery(id+"F0.wireOp",EDGE,"E1.top"),sQuery(id+"F0.wireOp",EDGE,"E1.left"),sQuery(id+"F0.wireOp",EDGE,"E2.bottom"),sQuery(id+"F0.wireOp",EDGE,"E2.left"),sQuery(id+"F0.wireOp",EDGE,"E2.right"),sQuery(id+"F0.wireOp",EDGE,"E3.bottom"),sQuery(id+"F0.wireOp",EDGE,"E3.left"),sQuery(id+"F0.wireOp",EDGE,"E3.right"),sQuery(id+"F0.wireOp",EDGE,"E4.bottom"),sQuery(id+"F0.wireOp",EDGE,"E4.top"),sQuery(id+"F0.wireOp",EDGE,"E4.left"),sQuery(id+"F0.wireOp",EDGE,"E5"),sQuery(id+"F0.wireOp",EDGE,"E6"),sQuery(id+"F0.wireOp",EDGE,"E7"),sQuery(id+"F0.wireOp",EDGE,"E8"),sQuery(id+"F0.wireOp",EDGE,"E12"),sQuery(id+"F0.wireOp",EDGE,"E13"),sQuery(id+"F0.wireOp",EDGE,"E14.0"),sQuery(id+"F0.wireOp",EDGE,"E14.1"),sQuery(id+"F0.wireOp",EDGE,"E14.2"),sQuery(id+"F0.wireOp",EDGE,"E14.3"),sQuery(id+"F0.wireOp",EDGE,"E14.4"),sQuery(id+"F0.wireOp",EDGE,"E14.5"),sQuery(id+"F0.wireOp",EDGE,"E14.6"),subQ2,sQuery(id+"F0.wireOp",EDGE,"E14.8"),sQuery(id+"F0.wireOp",EDGE,"E14.9"),sQuery(id+"F0.wireOp",EDGE,"E14.10"),sQuery(id+"F0.wireOp",EDGE,"E14.11"),sQuery(id+"F0.wireOp",EDGE,"E16"),sQuery(id+"F0.wireOp",EDGE,"E17"),sQuery(id+"F0.wireOp",EDGE,"E19"),sQuery(id+"F0.wireOp",EDGE,"E20"),sQuery(id+"F0.wireOp",EDGE,"E22.0"),sQuery(id+"F0.wireOp",EDGE,"E23.0"),sQuery(id+"F0.wireOp",EDGE,"7QYkWqvo-aJCI-HwU7-Pkr0-dl33K8GSCUU7"),sQuery(id+"F0.wireOp",EDGE,"UtTPwMuY-yqNM-BxKw-NphB-S71OTgtlkQoO"),sQuery(id+"F0.wireOp",EDGE,"jUQw4thv-zTIx-3EJl-gbHM-SSJWuM9t6vhC"),sQuery(id+"F0.wireOp",EDGE,"jgdTeO3I-7sCt-ISHI-VTCF-wijFFm9s4p1R"),subQ1,sQuery(id+"F0.wireOp",EDGE,"E25"),sQuery(id+"F0.wireOp",EDGE,"E26"),subQ0,sQuery(id+"F0.wireOp",EDGE,"E28"),sQuery(id+"F0.wireOp",EDGE,"E29")])],"isStart":false}),makeQuery(id+"F12.opExtrude","SWEPT_FACE",FACE,{"disambiguationData":[OSD([subQ2,subQ1,subQ0]),TDD([makeQuery(id+"F11.imprint","IMPRINT",EDGE,{"disambiguationData":[TD([[makeQuery(id+"F11.imprint","INTERSECT",VERTEX,{"derivedFrom":[subQ3,sQuery(id+"F11.wireOp",EDGE,"E43")]}),1.0]])],"derivedFrom":subQ3})])]}),makeQuery(id+"F12.opExtrude","SWEPT_FACE",FACE,{"disambiguationData":[OSD([subQ2,subQ1,subQ0]),TDD([makeQuery(id+"F11.imprint","IMPRINT",EDGE,{"disambiguationData":[TD([[makeQuery(id+"F11.imprint","INTERSECT",VERTEX,{"derivedFrom":[subQ3,sQuery(id+"F11.wireOp",EDGE,"E44")]}),-1.0]])],"derivedFrom":subQ3})])]})]});}
            var sketch = newSketch(context, id + "F15", { "sketchPlane" : qUnion([Q0])});
            skLineSegment(sketch, "E47", {"start": v(38.68, -0.55) * mm, "end": v(38.68, 4.37) * mm, "construction": true});
            skLineSegment(sketch, "E48", {"start": v(-0.55, 38.68) * mm, "end": v(4.37, 38.68) * mm, "construction": true});
            skCircle(sketch, "E49", {"center": v(1.9, 38.68) * mm, "radius": 3.25 * mm});
            skCircle(sketch, "E50", {"center": v(38.68, 1.9) * mm, "radius": 3.25 * mm});
            skLineSegment(sketch, "E51", {"start": v(1.9, 38.68) * mm, "end": v(-42.92, -6.15) * mm, "construction": true});
            skLineSegment(sketch, "E52", {"start": v(38.68, 1.9) * mm, "end": v(-6.15, -42.92) * mm, "construction": true});
            skLineSegment(sketch, "E53", {"start": v(-29.84, -19.23) * mm, "end": v(-6.15, -42.92) * mm, "construction": true});
            skLineSegment(sketch, "E54", {"start": v(-29.84, -19.23) * mm, "end": v(-42.92, -6.15) * mm, "construction": true});
            skCircle(sketch, "E55", {"center": v(-6.15, -33.02) * mm, "radius": 3.25 * mm});
            skCircle(sketch, "E56", {"center": v(-33.02, -6.15) * mm, "radius": 3.25 * mm});
            skLineSegment(sketch, "E57.0", {"start": v(33.73, 6.86) * mm, "end": v(-11.1, -37.97) * mm, "construction": true});
            skLineSegment(sketch, "E58.0", {"start": v(6.86, 33.73) * mm, "end": v(-37.97, -11.1) * mm, "construction": true});
            skSolve(sketch);
        }
        {
            var Q0;
            Q0=makeQuery(id+"F15.imprint","IMPRINT",FACE,{"disambiguationData":[TD([[makeQuery(id+"F15.imprint","IMPRINT",EDGE,{"derivedFrom":sQuery(id+"F15.wireOp",EDGE,"E50")}),1.0]])]});
            var Q1;
            Q1=makeQuery(id+"F15.imprint","IMPRINT",FACE,{"disambiguationData":[TD([[makeQuery(id+"F15.imprint","IMPRINT",EDGE,{"derivedFrom":sQuery(id+"F15.wireOp",EDGE,"E49")}),1.0]])]});
            var Q2;
            Q2=makeQuery(id+"F15.imprint","IMPRINT",FACE,{"disambiguationData":[TD([[makeQuery(id+"F15.imprint","IMPRINT",EDGE,{"derivedFrom":sQuery(id+"F15.wireOp",EDGE,"E55")}),1.0]])]});
            var Q3;
            Q3=makeQuery(id+"F15.imprint","IMPRINT",FACE,{"disambiguationData":[TD([[makeQuery(id+"F15.imprint","IMPRINT",EDGE,{"derivedFrom":sQuery(id+"F15.wireOp",EDGE,"E56")}),1.0]])]});
            extrude(context, id + "F16", {"entities" : qUnion([Q0, Q1, Q2, Q3]), "operationType" : NewBodyOperationType.REMOVE, "oppositeDirection" : true, "depth" : 15 * mm});
        }
    });
